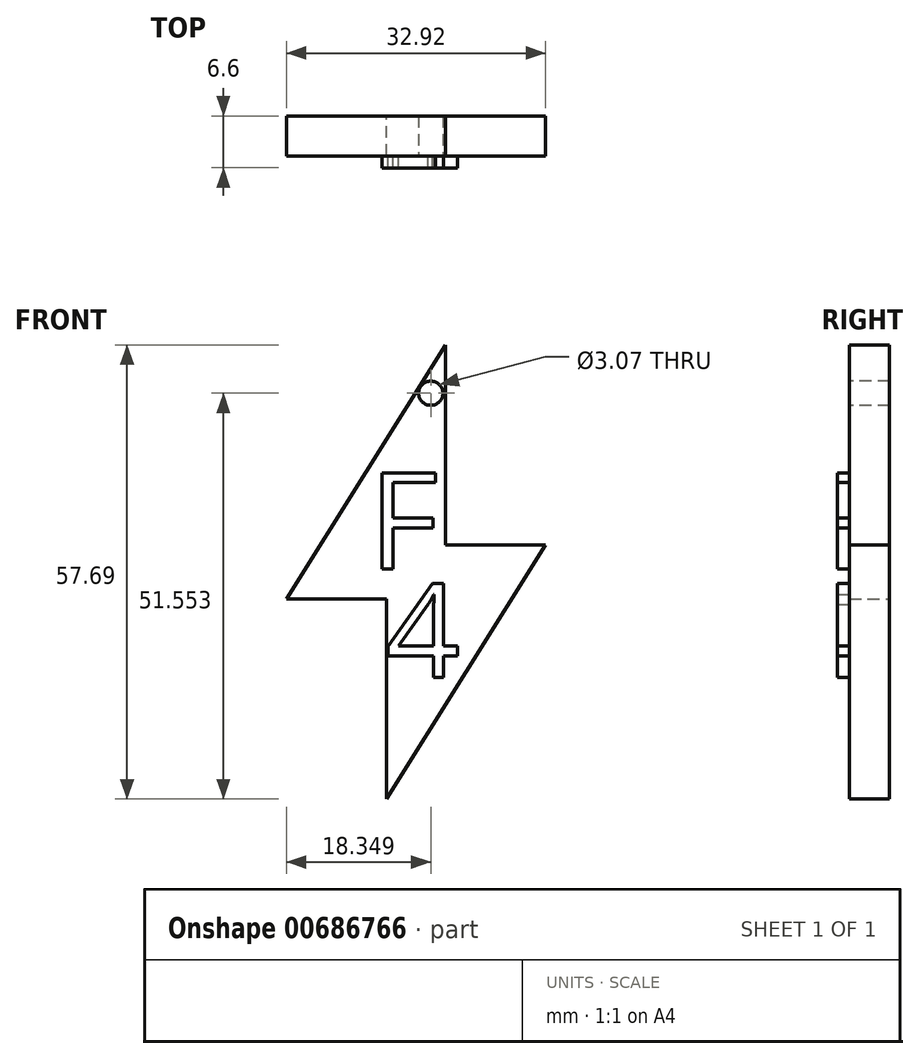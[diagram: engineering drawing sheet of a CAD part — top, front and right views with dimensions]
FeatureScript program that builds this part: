
annotation { "Feature Type Name" : "Feature", "Feature Type Description" : "" }
export const myFeature = defineFeature(function(context is Context, id is Id, definition is map)
    precondition{}
    {
        {
            var Q0;
            Q0=qCreatedBy(makeId("Front.planeOp"),FACE);
            var sketch = newSketch(context, id + "F0", { "sketchPlane" : qUnion([Q0])});
            skLineSegment(sketch, "E0", {"start": v(9.74, 13.1) * mm, "end": v(9.74, -12.3) * mm});
            skLineSegment(sketch, "E1", {"start": v(9.74, -12.3) * mm, "end": v(22.44, -12.3) * mm});
            skLineSegment(sketch, "E2", {"start": v(22.44, -12.3) * mm, "end": v(2.22, -44.6) * mm});
            skLineSegment(sketch, "E3", {"start": v(2.22, -44.6) * mm, "end": v(2.22, -19.2) * mm});
            skLineSegment(sketch, "E4", {"start": v(2.22, -19.2) * mm, "end": v(-10.48, -19.2) * mm});
            skLineSegment(sketch, "E5", {"start": v(-10.48, -19.2) * mm, "end": v(9.74, 13.1) * mm});
            skSolve(sketch);
        }
        {
            var Q0;
            Q0=makeQuery(id+"F0.imprint","IMPRINT",FACE,{"disambiguationData":[TD([[makeQuery(id+"F0.imprint","IMPRINT",EDGE,{"derivedFrom":sQuery(id+"F0.wireOp",EDGE,"E0")}),-1.0]])]});
            extrude(context, id + "F1", {"entities" : qUnion([Q0]), "depth" : 5.08 * mm, "offsetDistance" : 25.4 * mm});
        }
        {
            var Q0;
            Q0=makeQuery(id+"F1.opExtrude","CAP_FACE",FACE,{"disambiguationData":[OSD([sQuery(id+"F0.wireOp",EDGE,"E0"),sQuery(id+"F0.wireOp",EDGE,"E1"),sQuery(id+"F0.wireOp",EDGE,"E2"),sQuery(id+"F0.wireOp",EDGE,"E3"),sQuery(id+"F0.wireOp",EDGE,"E4"),sQuery(id+"F0.wireOp",EDGE,"E5")])],"isStart":false});
            var sketch = newSketch(context, id + "F2", { "sketchPlane" : qUnion([Q0])});
            skText(sketch, "E6", { "text": "F\n", "fontName": "OpenSans-Regular.ttf"});
            skPoint(sketch, "E6.firstSnap0", {"position": v(-0.37, -3.05) * mm});
            const initialGuessF2  = {"E6": [0, -0.01535, 1, 0, 0.0123]};
            skSetInitialGuess(sketch, initialGuessF2);
            skSolve(sketch);
        }
        {
            var Q0;
            Q0=makeQuery(id+"F2.imprint","IMPRINT",FACE,{"disambiguationData":[TD([[makeQuery(id+"F2.imprint","IMPRINT",EDGE,{"derivedFrom":sQuery(id+"F2.wireOp",EDGE,"E6.sketch_text.stroke-0")}),1.0]])]});
            var sketch = newSketch(context, id + "F3", { "sketchPlane" : qUnion([Q0])});
            skText(sketch, "E7", { "text": "4\n", "fontName": "OpenSans-Regular.ttf"});
            const initialGuessF3  = {"E7": [0.0021, -0.02913, 1, 0, 0.01196]};
            skSetInitialGuess(sketch, initialGuessF3);
            skSolve(sketch);
        }
        {
            var Q0;
            Q0 = qSketchRegion(id + "F2", true);
            extrude(context, id + "F4", {"entities" : qUnion([Q0]), "operationType" : NewBodyOperationType.ADD, "depth" : 1.52 * mm, "offsetDistance" : 25.4 * mm});
        }
        {
            var Q0;
            Q0 = qSketchRegion(id + "F3", true);
            extrude(context, id + "F5", {"entities" : qUnion([Q0]), "operationType" : NewBodyOperationType.ADD, "depth" : 1.52 * mm, "offsetDistance" : 25.4 * mm});
        }
        {
            var Q0;
            {var subQ0=sQuery(id+"F0.wireOp",EDGE,"E2");var subQ1=sQuery(id+"F0.wireOp",EDGE,"E3");var subQ2=sQuery(id+"F0.wireOp",EDGE,"E0");var subQ3=sQuery(id+"F0.wireOp",EDGE,"E4");var subQ4=sQuery(id+"F0.wireOp",EDGE,"E5");var subQ5=sQuery(id+"F0.wireOp",EDGE,"E1");Q0=makeQuery(id+"F5.boolean.opBoolean","SPLIT",FACE,{"disambiguationData":[TD([makeQuery(id+"F1.opExtrude","SWEPT_FACE",FACE,{"disambiguationData":[OSD([subQ2])]})])],"derivedFrom":makeQuery(id+"F1.opExtrude","CAP_FACE",FACE,{"disambiguationData":[OSD([subQ2,subQ5,subQ0,subQ1,subQ3,subQ4])],"isStart":false})});}
            var sketch = newSketch(context, id + "F6", { "sketchPlane" : qUnion([Q0])});
            skCircle(sketch, "E8", {"center": v(7.87, 6.95) * mm, "radius": 1.54 * mm});
            skSolve(sketch);
        }
        {
            var Q0;
            Q0=makeQuery(id+"F6.imprint","IMPRINT",FACE,{"disambiguationData":[TD([[makeQuery(id+"F6.imprint","IMPRINT",EDGE,{"derivedFrom":sQuery(id+"F6.wireOp",EDGE,"E8")}),1.0]])]});
            extrude(context, id + "F7", {"entities" : qUnion([Q0]), "operationType" : NewBodyOperationType.REMOVE, "oppositeDirection" : true, "depth" : 25.4 * mm, "offsetDistance" : 25.4 * mm});
        }
    });
